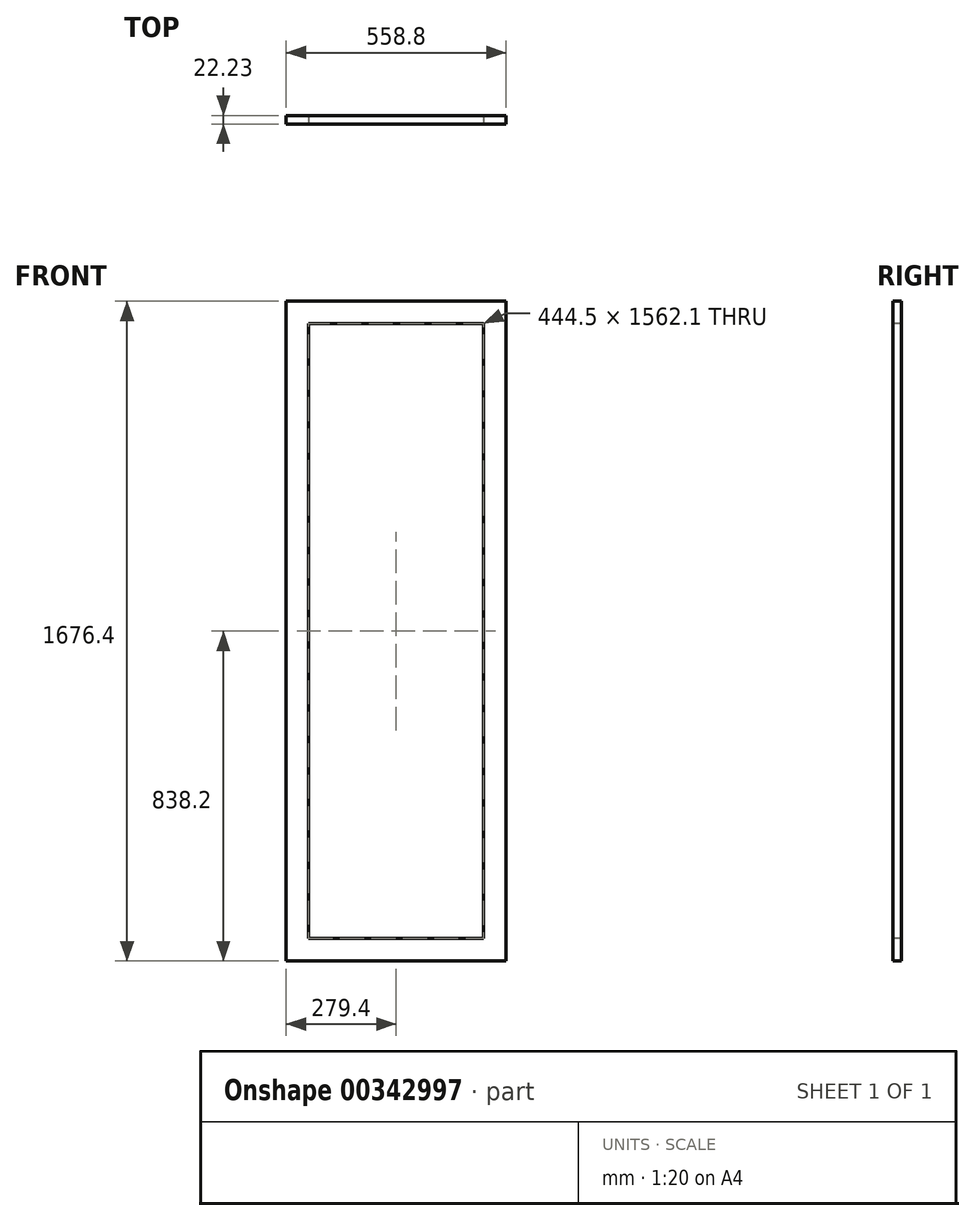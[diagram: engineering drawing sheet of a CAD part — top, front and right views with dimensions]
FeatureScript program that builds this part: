
annotation { "Feature Type Name" : "Feature", "Feature Type Description" : "" }
export const myFeature = defineFeature(function(context is Context, id is Id, definition is map)
    precondition{}
    {
        {
            var Q0;
            Q0=qCreatedBy(makeId("Front.planeOp"),FACE);
            var sketch = newSketch(context, id + "F0", { "sketchPlane" : qUnion([Q0])});
            skLineSegment(sketch, "E0.bottom", {"start": v(-279.4, 838.2) * mm, "end": v(279.4, 838.2) * mm});
            skLineSegment(sketch, "E0.top", {"start": v(-279.4, -838.2) * mm, "end": v(279.4, -838.2) * mm});
            skLineSegment(sketch, "E0.left", {"start": v(-279.4, 838.2) * mm, "end": v(-279.4, -838.2) * mm});
            skLineSegment(sketch, "E0.right", {"start": v(279.4, 838.2) * mm, "end": v(279.4, -838.2) * mm});
            skLineSegment(sketch, "E1", {"start": v(-279.4, 838.2) * mm, "end": v(279.4, -838.2) * mm, "construction": true});
            skLineSegment(sketch, "E2.0", {"start": v(-222.25, -781.05) * mm, "end": v(222.25, -781.05) * mm});
            skLineSegment(sketch, "E2.1", {"start": v(-222.25, 781.05) * mm, "end": v(-222.25, -781.05) * mm});
            skLineSegment(sketch, "E2.2", {"start": v(-222.25, 781.05) * mm, "end": v(222.25, 781.05) * mm});
            skLineSegment(sketch, "E2.3", {"start": v(222.25, 781.05) * mm, "end": v(222.25, -781.05) * mm});
            skSolve(sketch);
        }
        {
            var Q0;
            Q0 = qSketchRegion(id + "F0", true);
            extrude(context, id + "F1", {"entities" : qUnion([Q0]), "oppositeDirection" : true, "depth" : 22.22 * mm});
        }
    });
